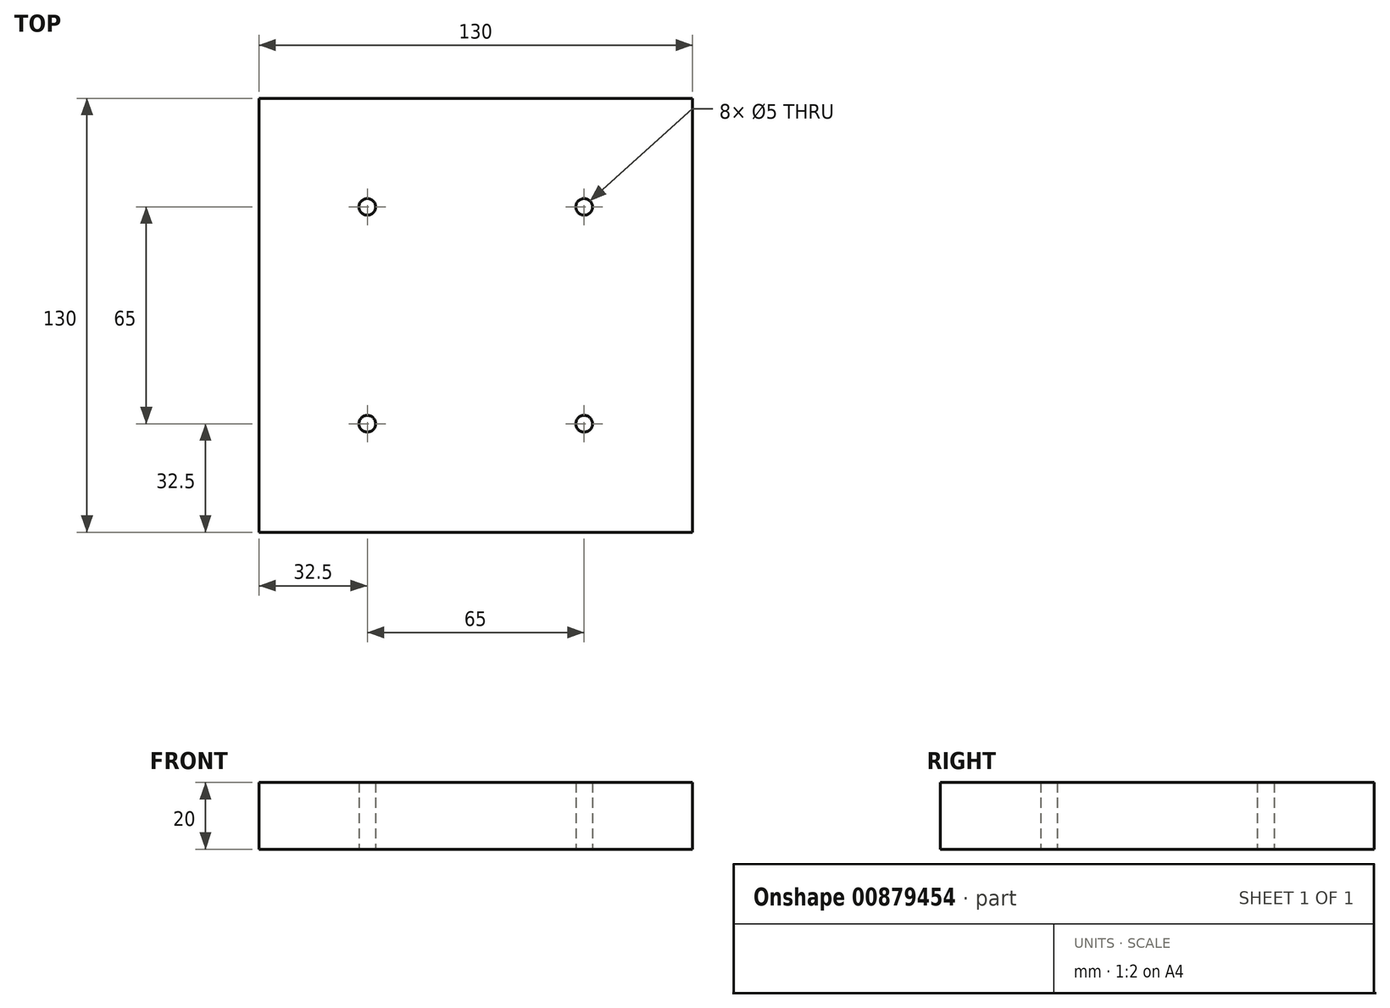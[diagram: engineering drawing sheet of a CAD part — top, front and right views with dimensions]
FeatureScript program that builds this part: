
annotation { "Feature Type Name" : "Feature", "Feature Type Description" : "" }
export const myFeature = defineFeature(function(context is Context, id is Id, definition is map)
    precondition{}
    {
        {
            var Q0;
            Q0=qCreatedBy(makeId("Top.planeOp"),FACE);
            var sketch = newSketch(context, id + "F0", { "sketchPlane" : qUnion([Q0])});
            skLineSegment(sketch, "E0.bottom", {"start": v(65, 65) * mm, "end": v(-65, 65) * mm});
            skLineSegment(sketch, "E0.top", {"start": v(65, -65) * mm, "end": v(-65, -65) * mm});
            skLineSegment(sketch, "E0.left", {"start": v(65, 65) * mm, "end": v(65, -65) * mm});
            skLineSegment(sketch, "E0.right", {"start": v(-65, 65) * mm, "end": v(-65, -65) * mm});
            skPoint(sketch, "E0.middle", {"position": v(0, 0) * mm});
            skCircle(sketch, "E1", {"center": v(-32.5, 32.5) * mm, "radius": 2.5 * mm});
            skLineSegment(sketch, "E2", {"start": v(0, 65) * mm, "end": v(0, 0) * mm, "construction": true});
            skLineSegment(sketch, "E3", {"start": v(-65, 0) * mm, "end": v(0, 0) * mm, "construction": true});
            skLineSegment(sketch, "E4", {"start": v(0, 0) * mm, "end": v(0, -65) * mm, "construction": true});
            skLineSegment(sketch, "E5", {"start": v(0, 0) * mm, "end": v(65, 0) * mm, "construction": true});
            skPoint(sketch, "E6", {"position": v(-32.5, 0) * mm});
            skPoint(sketch, "E7", {"position": v(0, 32.5) * mm});
            skPoint(sketch, "E8", {"position": v(32.5, 0) * mm});
            skPoint(sketch, "E9", {"position": v(0, -32.5) * mm});
            skCircle(sketch, "E10.MirrorC", {"center": v(32.5, 32.5) * mm, "radius": 2.5 * mm});
            skCircle(sketch, "E11.MirrorC", {"center": v(32.5, -32.5) * mm, "radius": 2.5 * mm});
            skCircle(sketch, "E12.MirrorC", {"center": v(-32.5, -32.5) * mm, "radius": 2.5 * mm});
            skSolve(sketch);
        }
        {
            var Q0;
            Q0=makeQuery(id+"F0.imprint","IMPRINT",FACE,{"disambiguationData":[TD([[makeQuery(id+"F0.imprint","IMPRINT",EDGE,{"derivedFrom":sQuery(id+"F0.wireOp",EDGE,"E0.bottom")}),1.0]])]});
            extrude(context, id + "F1", {"entities" : qUnion([Q0]), "endBound" : BoundingType.SYMMETRIC, "depth" : 20 * mm, "offsetDistance" : 25 * mm});
        }
        {
            var Q0;
            Q0=makeQuery(id+"F1.opExtrude","SWEPT_FACE",FACE,{"disambiguationData":[OSD([sQuery(id+"F0.wireOp",EDGE,"E0.left")])]});
            var sketch = newSketch(context, id + "F2", { "sketchPlane" : qUnion([Q0])});
            skCircle(sketch, "E13", {"center": v(-45, 0) * mm, "radius": 5 * mm});
            skLineSegment(sketch, "E14", {"start": v(0, 10) * mm, "end": v(0, -10) * mm, "construction": true});
            skCircle(sketch, "E15.MirrorC", {"center": v(45, 0) * mm, "radius": 5 * mm});
            skSolve(sketch);
        }
    });
